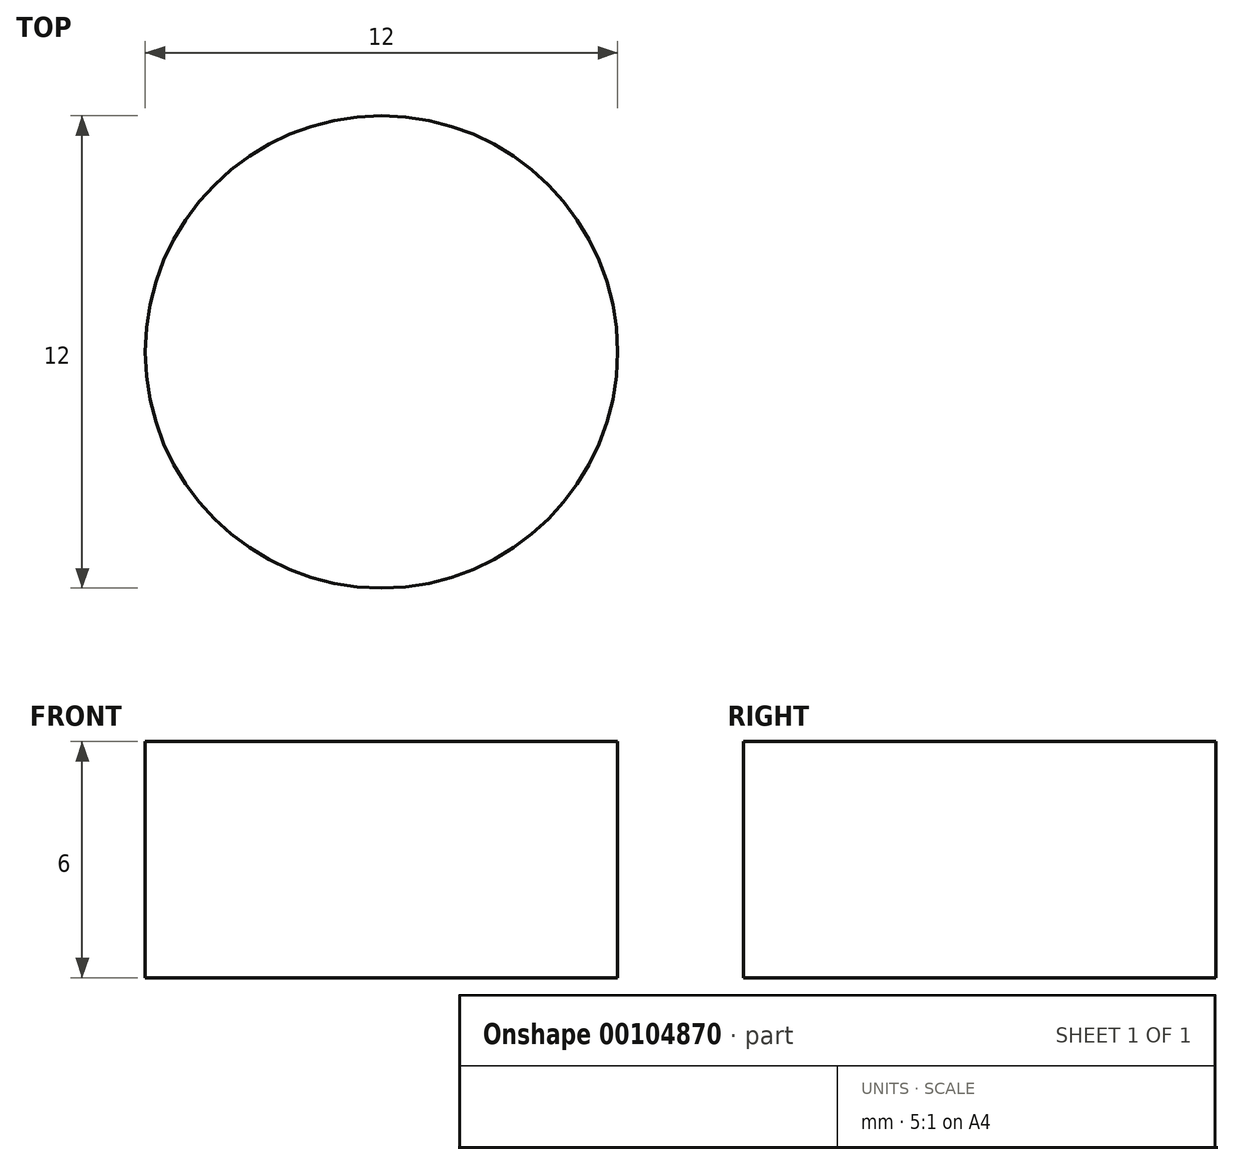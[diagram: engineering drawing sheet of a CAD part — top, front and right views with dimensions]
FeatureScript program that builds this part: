
annotation { "Feature Type Name" : "Feature", "Feature Type Description" : "" }
export const myFeature = defineFeature(function(context is Context, id is Id, definition is map)
    precondition{}
    {
        {
            var Q0;
            Q0=qCreatedBy(makeId("Top.planeOp"),FACE);
            var sketch = newSketch(context, id + "F0", { "sketchPlane" : qUnion([Q0])});
            skCircle(sketch, "E0", {"center": v(0, 0) * mm, "radius": 6 * mm});
            skSolve(sketch);
        }
        {
            var Q0;
            Q0=makeQuery(id+"F0.imprint","IMPRINT",FACE,{"disambiguationData":[TD([[makeQuery(id+"F0.imprint","IMPRINT",EDGE,{"derivedFrom":sQuery(id+"F0.wireOp",EDGE,"E0")}),1.0]])]});
            extrude(context, id + "F1", {"entities" : qUnion([Q0]), "depth" : 6 * mm});
        }
    });
